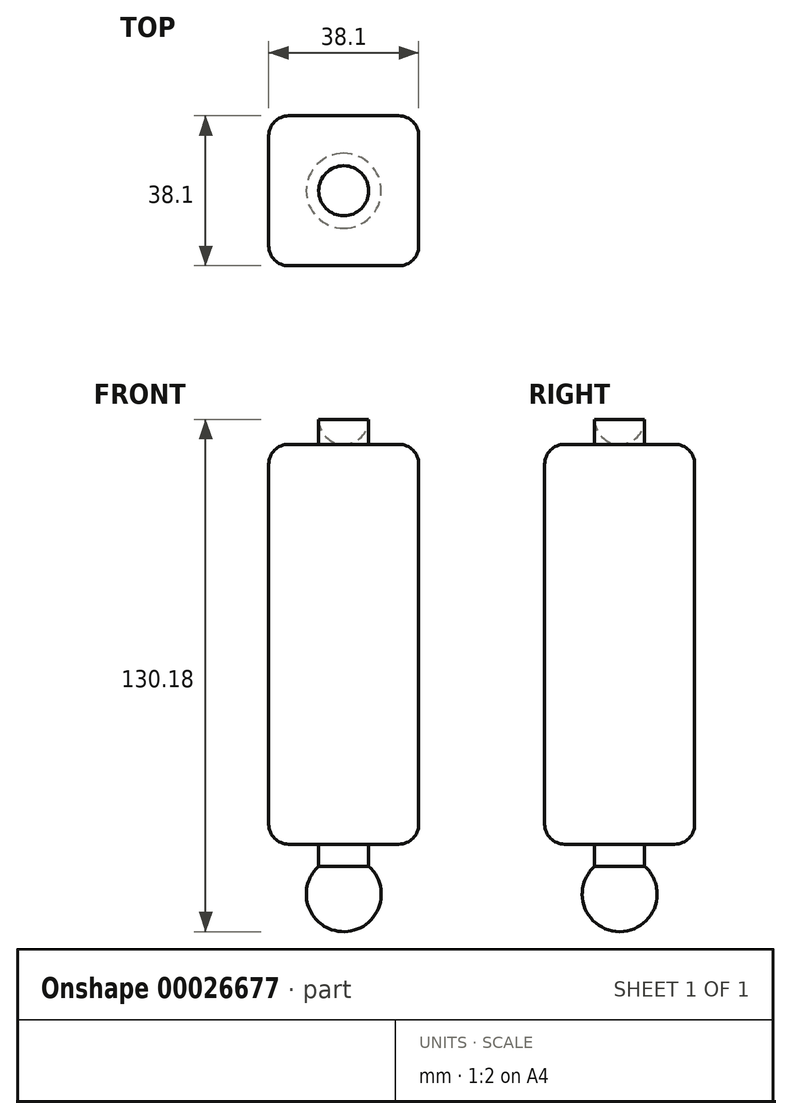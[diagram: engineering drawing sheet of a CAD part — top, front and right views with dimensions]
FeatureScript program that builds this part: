
annotation { "Feature Type Name" : "Feature", "Feature Type Description" : "" }
export const myFeature = defineFeature(function(context is Context, id is Id, definition is map)
    precondition{}
    {
        {
            var Q0;
            Q0=qCreatedBy(makeId("Top.planeOp"),FACE);
            var sketch = newSketch(context, id + "F0", { "sketchPlane" : qUnion([Q0])});
            skLineSegment(sketch, "E0.rect.bottom", {"start": v(-19.05, -19.05) * mm, "end": v(19.05, -19.05) * mm});
            skLineSegment(sketch, "E0.rect.top", {"start": v(-19.05, 19.05) * mm, "end": v(19.05, 19.05) * mm});
            skLineSegment(sketch, "E0.rect.left", {"start": v(-19.05, -19.05) * mm, "end": v(-19.05, 19.05) * mm});
            skLineSegment(sketch, "E0.rect.right", {"start": v(19.05, -19.05) * mm, "end": v(19.05, 19.05) * mm});
            skPoint(sketch, "E0.rect.middle", {"position": v(0, 0) * mm});
            skSolve(sketch);
        }
        {
            var Q0;
            Q0=makeQuery(id+"F0.imprint","IMPRINT",FACE,{"disambiguationData":[TD([[makeQuery(id+"F0.imprint","IMPRINT",EDGE,{"derivedFrom":sQuery(id+"F0.wireOp",EDGE,"E0.rect.bottom")}),1.0]])]});
            extrude(context, id + "F1", {"entities" : qUnion([Q0]), "depth" : 101.6 * mm});
        }
        {
            var Q0;
            Q0=makeQuery(id+"F1.opExtrude","CAP_EDGE",EDGE,{"disambiguationData":[OSD([sQuery(id+"F0.wireOp",EDGE,"E0.rect.bottom")])],"isStart":false});
            var Q1;
            Q1=makeQuery(id+"F1.opExtrude","CAP_EDGE",EDGE,{"disambiguationData":[OSD([sQuery(id+"F0.wireOp",EDGE,"E0.rect.right")])],"isStart":false});
            var Q2;
            Q2=makeQuery(id+"F1.opExtrude","SWEPT_EDGE",EDGE,{"disambiguationData":[OSD([sQuery(id+"F0.wireOp",EDGE,"E0.rect.bottom"),sQuery(id+"F0.wireOp",EDGE,"E0.rect.right")])]});
            var Q3;
            Q3=makeQuery(id+"F1.opExtrude","SWEPT_EDGE",EDGE,{"disambiguationData":[OSD([sQuery(id+"F0.wireOp",EDGE,"E0.rect.bottom"),sQuery(id+"F0.wireOp",EDGE,"E0.rect.left")])]});
            var Q4;
            Q4=makeQuery(id+"F1.opExtrude","SWEPT_EDGE",EDGE,{"disambiguationData":[OSD([sQuery(id+"F0.wireOp",EDGE,"E0.rect.top"),sQuery(id+"F0.wireOp",EDGE,"E0.rect.right")])]});
            var Q5;
            Q5=makeQuery(id+"F1.opExtrude","CAP_EDGE",EDGE,{"disambiguationData":[OSD([sQuery(id+"F0.wireOp",EDGE,"E0.rect.top")])],"isStart":false});
            var Q6;
            Q6=makeQuery(id+"F1.opExtrude","CAP_EDGE",EDGE,{"disambiguationData":[OSD([sQuery(id+"F0.wireOp",EDGE,"E0.rect.left")])],"isStart":false});
            var Q7;
            Q7=makeQuery(id+"F1.opExtrude","CAP_EDGE",EDGE,{"disambiguationData":[OSD([sQuery(id+"F0.wireOp",EDGE,"E0.rect.top")])],"isStart":true});
            var Q8;
            Q8=makeQuery(id+"F1.opExtrude","CAP_EDGE",EDGE,{"disambiguationData":[OSD([sQuery(id+"F0.wireOp",EDGE,"E0.rect.left")])],"isStart":true});
            var Q9;
            Q9=makeQuery(id+"F1.opExtrude","CAP_EDGE",EDGE,{"disambiguationData":[OSD([sQuery(id+"F0.wireOp",EDGE,"E0.rect.bottom")])],"isStart":true});
            var Q10;
            Q10=makeQuery(id+"F1.opExtrude","CAP_EDGE",EDGE,{"disambiguationData":[OSD([sQuery(id+"F0.wireOp",EDGE,"E0.rect.right")])],"isStart":true});
            var Q11;
            Q11=makeQuery(id+"F1.opExtrude","SWEPT_EDGE",EDGE,{"disambiguationData":[OSD([sQuery(id+"F0.wireOp",EDGE,"E0.rect.top"),sQuery(id+"F0.wireOp",EDGE,"E0.rect.left")])]});
            fillet(context, id + "F2", {"entities" : qUnion([Q0, Q1, Q2, Q3, Q4, Q5, Q6, Q7, Q8, Q9, Q10, Q11]), "radius" : 5.08 * mm, "tangentPropagation" : true, "allowEdgeOverflow" : false});
        }
        {
            var Q0;
            Q0=makeQuery(id+"F1.opExtrude","CAP_FACE",FACE,{"disambiguationData":[OSD([sQuery(id+"F0.wireOp",EDGE,"E0.rect.bottom"),sQuery(id+"F0.wireOp",EDGE,"E0.rect.top"),sQuery(id+"F0.wireOp",EDGE,"E0.rect.left"),sQuery(id+"F0.wireOp",EDGE,"E0.rect.right")])],"isStart":true});
            var sketch = newSketch(context, id + "F3", { "sketchPlane" : qUnion([Q0])});
            skCircle(sketch, "E1", {"center": v(0, 0) * mm, "radius": 6.35 * mm});
            skSolve(sketch);
        }
        {
            var Q0;
            Q0=makeQuery(id+"F3.imprint","IMPRINT",FACE,{"disambiguationData":[TD([[makeQuery(id+"F3.imprint","IMPRINT",EDGE,{"derivedFrom":sQuery(id+"F3.wireOp",EDGE,"E1")}),1.0]])]});
            extrude(context, id + "F4", {"entities" : qUnion([Q0]), "operationType" : NewBodyOperationType.ADD, "depth" : 12.7 * mm});
        }
        {
            var Q0;
            Q0=makeQuery(id+"F4.opExtrude","CAP_FACE",FACE,{"disambiguationData":[OSD([sQuery(id+"F3.wireOp",EDGE,"E1")])],"isStart":false});
            var sketch = newSketch(context, id + "F5", { "sketchPlane" : qUnion([Q0])});
            skCircle(sketch, "E2", {"center": v(0, 0) * mm, "radius": 9.53 * mm});
            skLineSegment(sketch, "E3", {"start": v(0, -9.53) * mm, "end": v(0, 9.53) * mm});
            skSolve(sketch);
        }
        {
            var Q0;
            Q0=makeQuery(id+"F1.opExtrude","CAP_FACE",FACE,{"disambiguationData":[OSD([sQuery(id+"F0.wireOp",EDGE,"E0.rect.bottom"),sQuery(id+"F0.wireOp",EDGE,"E0.rect.top"),sQuery(id+"F0.wireOp",EDGE,"E0.rect.left"),sQuery(id+"F0.wireOp",EDGE,"E0.rect.right")])],"isStart":false});
            var sketch = newSketch(context, id + "F6", { "sketchPlane" : qUnion([Q0])});
            skCircle(sketch, "E4", {"center": v(0, 0) * mm, "radius": 6.35 * mm});
            skSolve(sketch);
        }
        {
            var Q0;
            {var subQ0=makeQuery(id+"F4.opExtrude","CAP_EDGE",EDGE,{"disambiguationData":[OSD([sQuery(id+"F3.wireOp",EDGE,"E1")])],"isStart":false});var subQ1=sQuery(id+"F5.wireOp",EDGE,"E3");var subQ3=makeQuery(id+"F5.imprint","INTERSECT",VERTEX,{"disambiguationData":[OD(0.0)],"derivedFrom":[subQ0,subQ1]});Q0=makeQuery(id+"F5.imprint","IMPRINT",FACE,{"disambiguationData":[TD([[makeQuery(id+"F5.imprint","IMPRINT",EDGE,{"disambiguationData":[TD([[subQ3,-1.0]])],"derivedFrom":subQ1}),1.0]])]});}
            var Q1;
            {var subQ1=sQuery(id+"F5.wireOp",EDGE,"E3");var subQ4=sQuery(id+"F5.wireOp",EDGE,"E2");var subQ6=makeQuery(id+"F5.imprint","INTERSECT",VERTEX,{"disambiguationData":[OD(0.0)],"derivedFrom":[subQ4,subQ1]});Q1=makeQuery(id+"F5.imprint","IMPRINT",FACE,{"disambiguationData":[TD([[makeQuery(id+"F5.imprint","IMPRINT",EDGE,{"disambiguationData":[TD([[subQ6,1.0]])],"derivedFrom":subQ4}),1.0]])]});}
            var Q2;
            Q2=sQuery(id+"F5.wireOp",EDGE,"E3");
            revolve(context, id + "F7", {"operationType" : NewBodyOperationType.ADD, "entities" : qUnion([Q0, Q1]), "axis" : qUnion([Q2]), "revolveType" : RevolveType.FULL});
        }
        {
            var Q0;
            Q0=makeQuery(id+"F6.imprint","IMPRINT",FACE,{"disambiguationData":[TD([[makeQuery(id+"F6.imprint","IMPRINT",EDGE,{"derivedFrom":sQuery(id+"F6.wireOp",EDGE,"E4")}),1.0]])]});
            extrude(context, id + "F8", {"entities" : qUnion([Q0]), "operationType" : NewBodyOperationType.ADD, "depth" : 6.35 * mm});
        }
        {
            var Q0;
            Q0=makeQuery(id+"F8.opExtrude","CAP_FACE",FACE,{"disambiguationData":[OSD([sQuery(id+"F6.wireOp",EDGE,"E4")])],"isStart":false});
            var sketch = newSketch(context, id + "F9", { "sketchPlane" : qUnion([Q0])});
            skLineSegment(sketch, "E5", {"start": v(0, 6.35) * mm, "end": v(0, -6.35) * mm});
            skSolve(sketch);
        }
        {
            var Q0;
            {var subQ1=sQuery(id+"F9.wireOp",EDGE,"E5");Q0=makeQuery(id+"F9.imprint","IMPRINT",FACE,{"disambiguationData":[TD([[makeQuery(id+"F9.imprint","IMPRINT",EDGE,{"derivedFrom":subQ1}),-1.0]])]});}
            var Q1;
            Q1=sQuery(id+"F9.wireOp",EDGE,"E5");
            revolve(context, id + "F10", {"operationType" : NewBodyOperationType.REMOVE, "entities" : qUnion([Q0]), "axis" : qUnion([Q1]), "revolveType" : RevolveType.FULL});
        }
    });
